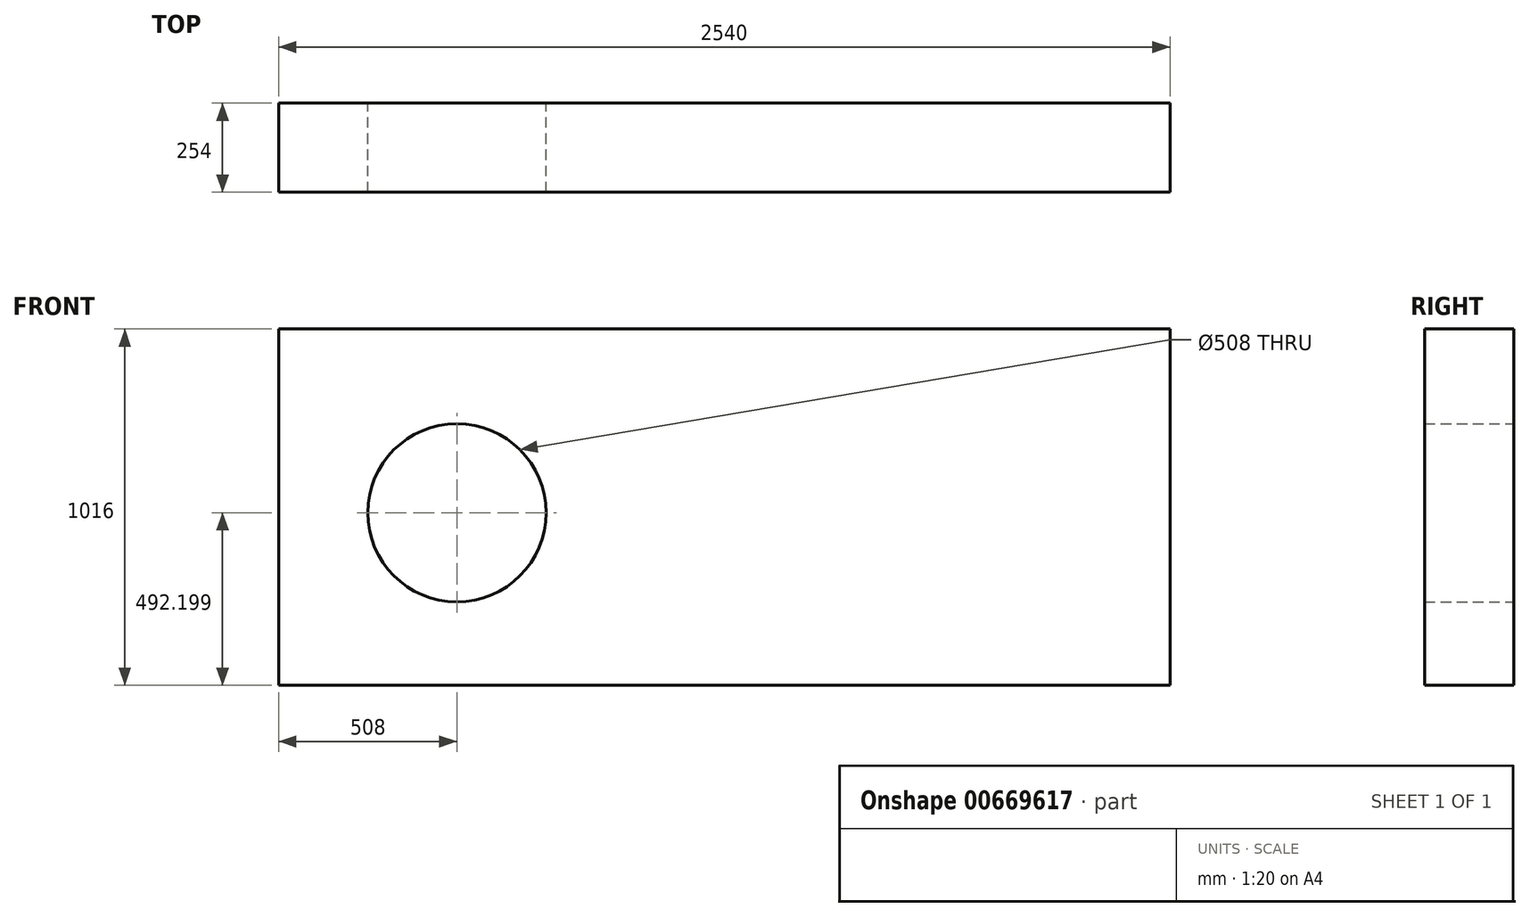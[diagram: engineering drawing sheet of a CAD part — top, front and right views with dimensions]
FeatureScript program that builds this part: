
annotation { "Feature Type Name" : "Feature", "Feature Type Description" : "" }
export const myFeature = defineFeature(function(context is Context, id is Id, definition is map)
    precondition{}
    {
        {
            var Q0;
            Q0=qCreatedBy(makeId("Front.planeOp"),FACE);
            var sketch = newSketch(context, id + "F0", { "sketchPlane" : qUnion([Q0])});
            skLineSegment(sketch, "E0.bottom", {"start": v(0, 0) * mm, "end": v(2540, 0) * mm});
            skLineSegment(sketch, "E0.top", {"start": v(0, 1016) * mm, "end": v(2540, 1016) * mm});
            skLineSegment(sketch, "E0.left", {"start": v(0, 0) * mm, "end": v(0, 1016) * mm});
            skLineSegment(sketch, "E0.right", {"start": v(2540, 0) * mm, "end": v(2540, 1016) * mm});
            skCircle(sketch, "E1", {"center": v(508, 492.2) * mm, "radius": 254 * mm});
            skSolve(sketch);
        }
        {
            var Q0;
            Q0=makeQuery(id+"F0.imprint","IMPRINT",FACE,{"disambiguationData":[TD([[makeQuery(id+"F0.imprint","IMPRINT",EDGE,{"derivedFrom":sQuery(id+"F0.wireOp",EDGE,"E0.bottom")}),1.0]])]});
            extrude(context, id + "F1", {"entities" : qUnion([Q0]), "depth" : 254 * mm, "offsetDistance" : 25.4 * mm});
        }
    });
